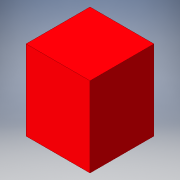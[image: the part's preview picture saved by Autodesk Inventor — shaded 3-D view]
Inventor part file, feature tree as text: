
AUTODESK INVENTOR PART (.ipt)
format: ipt  version: 2016 (Build 200138000, 138)  size: 90,112 bytes
history: native  units: in
note: dims shown in document units (in); Inventor stores cm internally (conversion verified against a paired STEP export)
features: extrude x1, sketch x1
ambient origin geometry x8: Origin, YZ Plane, XZ Plane, XY Plane, X Axis, Y Axis, Z Axis, Center Point
bodies: Solid1 (feature_tree)
feature tree (2):
  extrude  "Extrusion1"  Depth=1.25in
  sketch  "Sketch1"  dims[d0=1.0in d1=1.25in d2=1.0in d3=0.0in]
